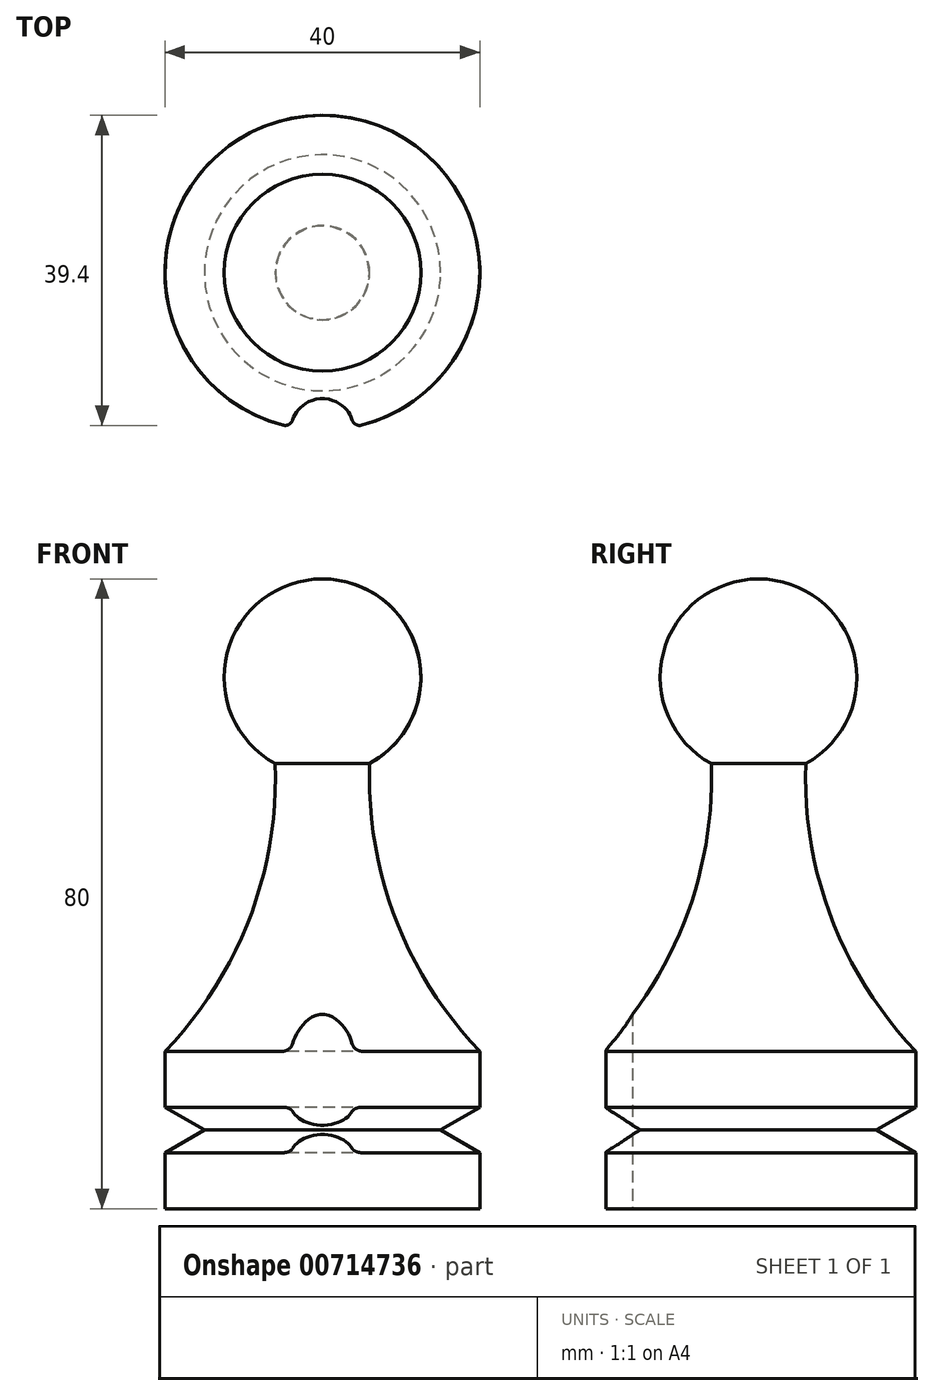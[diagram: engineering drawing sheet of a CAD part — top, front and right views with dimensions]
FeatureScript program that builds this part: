
annotation { "Feature Type Name" : "Feature", "Feature Type Description" : "" }
export const myFeature = defineFeature(function(context is Context, id is Id, definition is map)
    precondition{}
    {
        {
            var Q0;
            Q0=qCreatedBy(makeId("Front.planeOp"),FACE);
            var sketch = newSketch(context, id + "F0", { "sketchPlane" : qUnion([Q0])});
            skLineSegment(sketch, "E0", {"start": v(20, 0) * mm, "end": v(20, 7.11) * mm});
            skLineSegment(sketch, "E1", {"start": v(15, 10) * mm, "end": v(20, 7.11) * mm});
            skLineSegment(sketch, "E2", {"start": v(20, 12.89) * mm, "end": v(15, 10) * mm});
            skLineSegment(sketch, "E3", {"start": v(20, 12.89) * mm, "end": v(20, 20) * mm});
            skArc(sketch, "E4", {"start": v(6, 56.53) * mm, "mid": v(9.28, 36.84) * mm, "end": v(20, 20) * mm});
            skArc(sketch, "E5", {"start": v(6, 56.53) * mm, "mid": v(12.11, 70.6) * mm, "end": v(0, 80) * mm});
            skLineSegment(sketch, "E6", {"start": v(0, 80) * mm, "end": v(0, 0) * mm});
            skLineSegment(sketch, "E7", {"start": v(0, 0) * mm, "end": v(20, 0) * mm});
            skSolve(sketch);
        }
        {
            var Q0;
            Q0=makeQuery(id+"F0.imprint","IMPRINT",FACE,{"disambiguationData":[TD([[makeQuery(id+"F0.imprint","IMPRINT",EDGE,{"derivedFrom":sQuery(id+"F0.wireOp",EDGE,"E0")}),1.0]])]});
            var Q1;
            Q1=sQuery(id+"F0.wireOp",EDGE,"E6");
            revolve(context, id + "F1", {"entities" : qUnion([Q0]), "axis" : qUnion([Q1]), "revolveType" : RevolveType.FULL});
        }
        {
            var Q0;
            Q0=makeQuery(id+"F1.opRevolve","SWEPT_FACE",FACE,{"disambiguationData":[OSD([sQuery(id+"F0.wireOp",EDGE,"E7")])]});
            var sketch = newSketch(context, id + "F2", { "sketchPlane" : qUnion([Q0])});
            skCircle(sketch, "E8", {"center": v(0, 20) * mm, "radius": 4 * mm});
            skSolve(sketch);
        }
        {
            var Q0;
            Q0=qSketchRegion(id+"F2",true);
            extrude(context, id + "F3", {"entities" : qUnion([Q0]), "operationType" : NewBodyOperationType.REMOVE, "oppositeDirection" : true, "depth" : 30 * mm, "offsetDistance" : 25 * mm});
        }
        {
            var Q0;
            Q0=makeQuery(id+"F3.boolean.opBoolean","INTERSECT",EDGE,{"disambiguationData":[OD(0.0)],"derivedFrom":[makeQuery(id+"F1.opRevolve","SWEPT_FACE",FACE,{"disambiguationData":[OSD([sQuery(id+"F0.wireOp",EDGE,"E3")])]}),makeQuery(id+"F3.opExtrude","SWEPT_FACE",FACE,{"disambiguationData":[OSD([sQuery(id+"F2.wireOp",EDGE,"E8")])]})]});
            var Q1;
            Q1=makeQuery(id+"F3.boolean.opBoolean","INTERSECT",EDGE,{"disambiguationData":[OD(1.0)],"derivedFrom":[makeQuery(id+"F1.opRevolve","SWEPT_FACE",FACE,{"disambiguationData":[OSD([sQuery(id+"F0.wireOp",EDGE,"E3")])]}),makeQuery(id+"F3.opExtrude","SWEPT_FACE",FACE,{"disambiguationData":[OSD([sQuery(id+"F2.wireOp",EDGE,"E8")])]})]});
            var Q2;
            Q2=makeQuery(id+"F3.boolean.opBoolean","INTERSECT",EDGE,{"disambiguationData":[OD(0.0)],"derivedFrom":[makeQuery(id+"F1.opRevolve","SWEPT_FACE",FACE,{"disambiguationData":[OSD([sQuery(id+"F0.wireOp",EDGE,"E0")])]}),makeQuery(id+"F3.opExtrude","SWEPT_FACE",FACE,{"disambiguationData":[OSD([sQuery(id+"F2.wireOp",EDGE,"E8")])]})]});
            var Q3;
            Q3=makeQuery(id+"F3.boolean.opBoolean","INTERSECT",EDGE,{"disambiguationData":[OD(1.0)],"derivedFrom":[makeQuery(id+"F1.opRevolve","SWEPT_FACE",FACE,{"disambiguationData":[OSD([sQuery(id+"F0.wireOp",EDGE,"E0")])]}),makeQuery(id+"F3.opExtrude","SWEPT_FACE",FACE,{"disambiguationData":[OSD([sQuery(id+"F2.wireOp",EDGE,"E8")])]})]});
            fillet(context, id + "F4", {"entities" : qUnion([Q0, Q1, Q2, Q3]), "radius" : 1 * mm, "tangentPropagation" : true, "allowEdgeOverflow" : false});
        }
    });
